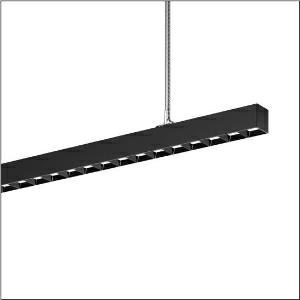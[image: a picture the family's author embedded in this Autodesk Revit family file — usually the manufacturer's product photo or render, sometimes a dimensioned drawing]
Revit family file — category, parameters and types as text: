
# Revit family: silica_r__21_51mx34dc3dbb_b9b0
name_source: partatom
category: Lighting Fixtures
units: mm (PartAtom-declared; Revit-internal decimal feet)

## family parameters
Cut with Voids When Loaded = No
Host = Face
Light Source = No
Part Type = Normal
Room Calculation Point = No
Round Connector Dimension = Use Diameter
Shared = No

## types (1)
- --- (1 x LED, 19200 lm, 129.1 W, 3000K)
    Apparent Load = 129 VA
    CIE Flux Codes = 74 94 99 56 100
    Color Rendering = 80
    Color Temperature = 3000K
    Default Elevation = 1800 mm
    Description = Silica® 21, office luminaire, primary light control with darklight reflector, of PMMA, black, light emission: direct/indirect distribution, primary light characteristic: asymmetric, installation type: suspended mounting, LED, rated luminous flux: 19.200lm, luminous efficacy: 149lm/W, light colour: 830, colour temperature: 3000K, with terminal, 3+2-pole, max. 2.5mm², mains connection: 220..240V, AC, 50/60Hz, rated input power: 129.1W, luminaire housing, of aluminium, jet black (RAL 9005), length: 3.004mm, width: 53mm, height: 53mm, protection rating (complete): IP20, insulation class (complete): insulation class I (protective earthing), certification: CE, permissible operating ambient temperature: 0..+35°C, standard: EN 50419, packaging unit: 1 piece
    Height = 53 mm
    Lamp = 1 x LED
    Lamp Light Flux = 19200 lm
    Lamp Power = 129.1 W
    Lamp count = 1
    Length = 3004 mm
    Luminous efficacy = 149 lm/W
    Manufacturer = Siteco
    ModVariant = No
    Model = 51MX34DC3DBB
    Mounting Place = Ceiling
    Mounting Type = Pendant
    Number of Poles = 1
    OnlyDefault = Yes
    Power Factor = 1
    Product Name = Silica® 21
    Product group = office luminaire | ceiling pendant
    ProductGroupID = 902
    Protection Class = Protection class I
    Protection Degree = IP 20
    RLX_Detail_Level = 1
    RLX_Emergency_Light_Flux = 0 lm
    RLX_Emergency_Type = 0
    RLX_Emergency_Type_DB = No
    RlxData = <blob elided: 67673 chars, md5=ad1aa22f>
    Socket = socket
    Standby Power = 0 W
    System Light Flux = 19200 lm
    System Power = 129 W
    Type Comments = factory setting: luminous flux: 100 % | dim-lin: 254 | 448 mA
    Type Image = l_1313617.jpg
    URL = http://relux.com
    VarID = @adj_068905
    Voltage = 0 V
    Weight = 0.00 kg
    Width = 53 mm

## geometry (parser evidence)
native form markers: Blend x4, Sweep x11
no freeform markers — native parametric forms only
